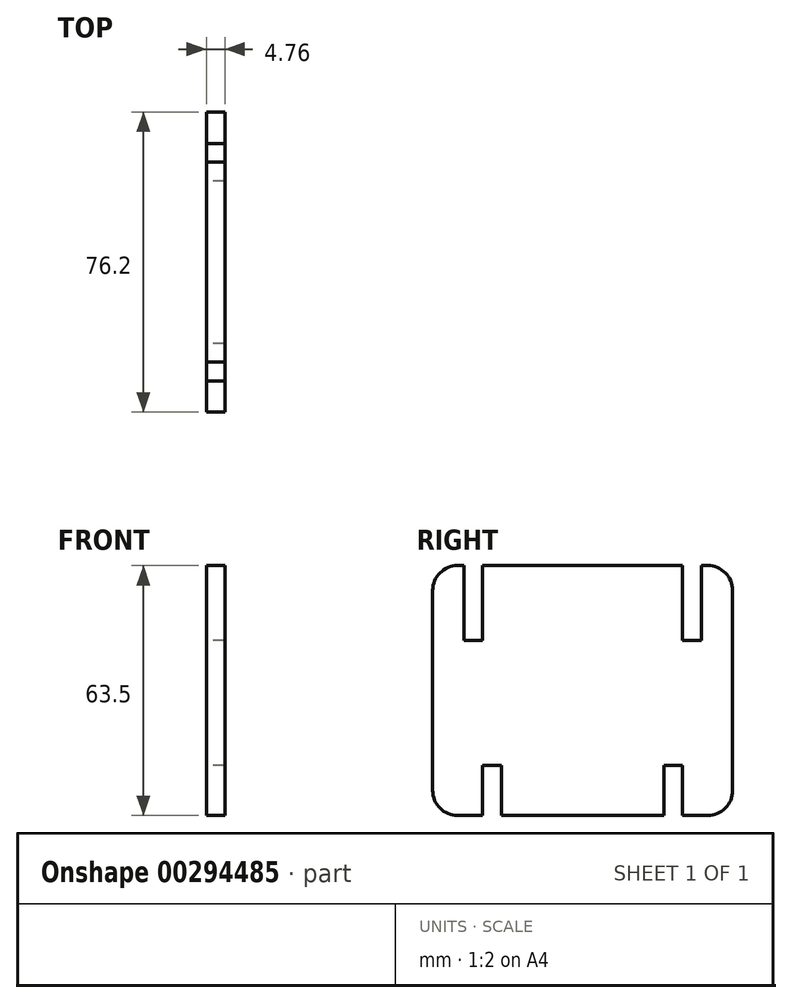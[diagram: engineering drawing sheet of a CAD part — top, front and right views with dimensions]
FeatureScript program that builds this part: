
annotation { "Feature Type Name" : "Feature", "Feature Type Description" : "" }
export const myFeature = defineFeature(function(context is Context, id is Id, definition is map)
    precondition{}
    {
        {
            var Q0;
            Q0=qCreatedBy(makeId("Right.planeOp"),FACE);
            var sketch = newSketch(context, id + "F0", { "sketchPlane" : qUnion([Q0])});
            skLineSegment(sketch, "E0.bottom", {"start": v(6.35, 0) * mm, "end": v(12.7, 0) * mm});
            skLineSegment(sketch, "E0.top", {"start": v(6.35, 63.5) * mm, "end": v(7.94, 63.5) * mm});
            skLineSegment(sketch, "E0.left", {"start": v(0, 6.35) * mm, "end": v(0, 57.15) * mm});
            skLineSegment(sketch, "E0.right", {"start": v(76.2, 6.35) * mm, "end": v(76.2, 57.15) * mm});
            skLineSegment(sketch, "E1", {"start": v(38.1, 63.5) * mm, "end": v(38.1, 0) * mm, "construction": true});
            skLineSegment(sketch, "E2.MirrorCS", {"start": v(63.5, 44.45) * mm, "end": v(68.26, 44.45) * mm});
            skLineSegment(sketch, "E3.MirrorCS", {"start": v(68.26, 63.5) * mm, "end": v(68.26, 44.45) * mm});
            skLineSegment(sketch, "E4.MirrorCS", {"start": v(63.5, 63.5) * mm, "end": v(63.5, 44.45) * mm});
            skLineSegment(sketch, "E5.trimOffspring", {"start": v(68.26, 63.5) * mm, "end": v(69.85, 63.5) * mm});
            skLineSegment(sketch, "E6.MirrorCS", {"start": v(12.7, 63.5) * mm, "end": v(12.7, 44.45) * mm});
            skLineSegment(sketch, "E7.MirrorCS", {"start": v(7.94, 63.5) * mm, "end": v(7.94, 44.45) * mm});
            skLineSegment(sketch, "E8.MirrorCS", {"start": v(12.7, 44.45) * mm, "end": v(7.94, 44.45) * mm});
            skLineSegment(sketch, "E9.trimOffspring", {"start": v(12.7, 63.5) * mm, "end": v(63.5, 63.5) * mm});
            skLineSegment(sketch, "E10.top", {"start": v(17.46, 12.7) * mm, "end": v(12.7, 12.7) * mm});
            skLineSegment(sketch, "E10.left", {"start": v(17.46, 0) * mm, "end": v(17.46, 12.7) * mm});
            skLineSegment(sketch, "E10.right", {"start": v(12.7, 0) * mm, "end": v(12.7, 12.7) * mm});
            skLineSegment(sketch, "E11.trimOffspring", {"start": v(17.46, 0) * mm, "end": v(58.74, 0) * mm});
            skLineSegment(sketch, "E12.MirrorCS", {"start": v(58.74, 0) * mm, "end": v(58.74, 12.7) * mm});
            skLineSegment(sketch, "E13.MirrorCS", {"start": v(58.74, 12.7) * mm, "end": v(63.5, 12.7) * mm});
            skLineSegment(sketch, "E14.MirrorCS", {"start": v(63.5, 0) * mm, "end": v(63.5, 12.7) * mm});
            skLineSegment(sketch, "E15.trimOffspring", {"start": v(63.5, 0) * mm, "end": v(69.85, 0) * mm});
            skPoint(sketch, "E16.visualSharp", {"position": v(0, 0) * mm});
            skArc(sketch, "E16.filletArc", {"start": v(0, 6.35) * mm, "mid": v(1.86, 1.86) * mm, "end": v(6.35, 0) * mm});
            skPoint(sketch, "E17.visualSharp", {"position": v(0, 63.5) * mm});
            skArc(sketch, "E17.filletArc", {"start": v(6.35, 63.5) * mm, "mid": v(1.86, 61.64) * mm, "end": v(0, 57.15) * mm});
            skPoint(sketch, "E18.visualSharp", {"position": v(76.2, 63.5) * mm});
            skArc(sketch, "E18.filletArc", {"start": v(76.2, 57.15) * mm, "mid": v(74.34, 61.64) * mm, "end": v(69.85, 63.5) * mm});
            skPoint(sketch, "E19.visualSharp", {"position": v(76.2, 0) * mm});
            skArc(sketch, "E19.filletArc", {"start": v(69.85, 0) * mm, "mid": v(74.34, 1.86) * mm, "end": v(76.2, 6.35) * mm});
            skSolve(sketch);
        }
        {
            var Q0;
            Q0=makeQuery(id+"F0.imprint","IMPRINT",FACE,{"disambiguationData":[TD([[makeQuery(id+"F0.imprint","IMPRINT",EDGE,{"derivedFrom":sQuery(id+"F0.wireOp",EDGE,"E0.bottom")}),1.0]])]});
            extrude(context, id + "F1", {"entities" : qUnion([Q0]), "depth" : 4.76 * mm});
        }
    });
